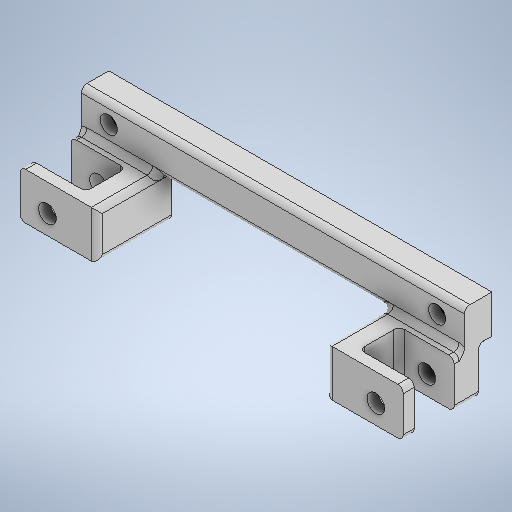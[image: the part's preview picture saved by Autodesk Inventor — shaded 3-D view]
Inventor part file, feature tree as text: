
AUTODESK INVENTOR PART (.ipt)
format: ipt  version: 2025.1 (Build 291241000, 241)  size: 362,496 bytes
history: native  units: mm
features: extrude x5, sketch x3, plane x1, fillet x1, mirror x1, projected_geometry x1
ambient origin geometry x8: Origin, YZ Plane, XZ Plane, XY Plane, X Axis, Y Axis, Z Axis, Center Point
bodies: Solid1 (feature_tree)
feature tree (12):
  sketch  "Sketch1"  dims[d0=4.85mm d1=30.0mm]
  extrude  "Extrusion1"  Depth=30.0mm
  extrude  "Extrusion2"  Depth=3.2mm
  extrude  "Extrusion3"  Depth=1.0mm
  extrude  "Extrusion4"  Depth=1.0mm
  plane  "Work Plane1"
  extrude  "Extrusion5"  TaperAngle=0.0deg  [1 undecoded]
  fillet  "Fillet1"  Radius=3.5mm
  mirror  "Mirror1"
  sketch  "Sketch2"  dims[d2=3.1mm d3=3.2mm]
  sketch  "Sketch4"  dims[d4=0.0mm d5=8.5mm d6=35.0mm d7=0.0mm d8=3.5mm d9=3.5mm d10=0.0mm d11=14.0mm d12=3.5mm d13=4.0mm d14=5.0mm d15=0.0mm d16=3.0mm d17=0.0mm d18=2.5mm d19=0.0mm d20=11.2mm d21=0.0mm d22=-2.0mm d23=5.0mm d24=7.3mm d25=0.0mm d26=1.0mm d28=0.5mm d29=0.872665mm d30=0.5mm d31=0.872665mm]
  projected_geometry  "Projected Loop1"
note: 1 required parameter value undecoded (feature->parameter linkage not recoverable at this tier; creation-order binding heuristic only, values carry confidence <= 0.55)
